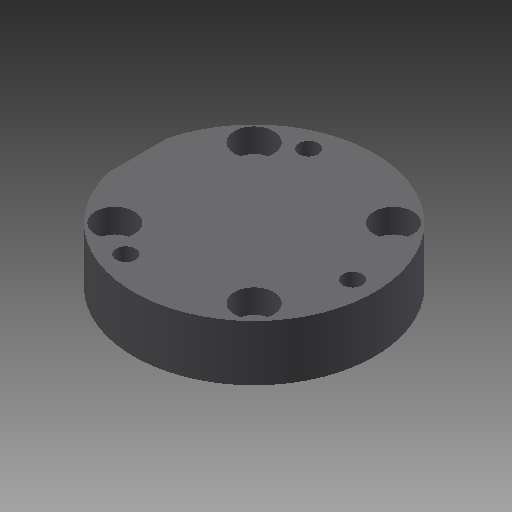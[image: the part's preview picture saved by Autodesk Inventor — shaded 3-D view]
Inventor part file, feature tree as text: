
AUTODESK INVENTOR PART (.ipt)
format: ipt  version: 2017 (Build 210142000, 142)  size: 270,336 bytes
history: native  units: in
note: dims shown in document units (in); Inventor stores cm internally (conversion verified against a paired STEP export)
features: other x287, sketch x9, hole x6, revolve x2, extrude x1, thread x1, pattern_linear x1
ambient origin geometry x8: Origin, YZ Plane, XZ Plane, XY Plane, X Axis, Y Axis, Z Axis, Center Point
bodies: Solid1 (feature_tree)
feature tree (307):
  revolve  "Revolution1"  [1 undecoded]
  extrude  "Extrusion1"  Depth=0.1091in TaperAngle=0.0deg
  revolve  "Revolution2"  [1 undecoded]
  thread  "Thread1"  [1 undecoded]
  hole  "Hole1"  [1 undecoded]
  hole  "Hole2"  [1 undecoded]
  hole  "Hole3"  [1 undecoded]
  hole  "Hole4"  [1 undecoded]
  hole  "Hole5"  [1 undecoded]
  hole  "Hole6"  [1 undecoded]
  pattern_linear  "Rectangular Pattern1"  [2 undecoded]
  other  "a1_XY"
  other  "a1_YZ"
  other  "a1_ZX"
  other  "a1_X"
  other  "a1_Y"
  other  "a1_Z"
  other  "a1_Center"
  other  "a2_XY"
  other  "a2_YZ"
  other  "a2_ZX"
  other  "a2_X"
  other  "a2_Y"
  other  "a2_Z"
  other  "a2_Center"
  other  "ar3_XY"
  other  "ar3_YZ"
  other  "ar3_ZX"
  other  "ar3_X"
  other  "ar3_Y"
  other  "ar3_Z"
  other  "ar3_Center"
  other  "ar4_XY"
  other  "ar4_YZ"
  other  "ar4_ZX"
  other  "ar4_X"
  other  "ar4_Y"
  other  "ar4_Z"
  other  "ar4_Center"
  other  "ar5_XY"
  other  "ar5_YZ"
  other  "ar5_ZX"
  other  "ar5_X"
  other  "ar5_Y"
  other  "ar5_Z"
  other  "ar5_Center"
  other  "ar6_XY"
  other  "ar6_YZ"
  other  "ar6_ZX"
  other  "ar6_X"
  other  "ar6_Y"
  other  "ar6_Z"
  other  "ar6_Center"
  other  "b1_XY"
  other  "b1_YZ"
  other  "b1_ZX"
  other  "b1_X"
  other  "b1_Y"
  other  "b1_Z"
  other  "b1_Center"
  other  "c11_XY"
  other  "c11_YZ"
  other  "c11_ZX"
  other  "c11_X"
  other  "c11_Y"
  other  "c11_Z"
  other  "c11_Center"
  other  "c22_XY"
  other  "c22_YZ"
  other  "c22_ZX"
  other  "c22_X"
  other  "c22_Y"
  other  "c22_Z"
  other  "c22_Center"
  other  "d11_XY"
  other  "d11_YZ"
  other  "d11_ZX"
  other  "d11_X"
  other  "d11_Y"
  other  "d11_Z"
  other  "d11_Center"
  other  "d22_XY"
  other  "d22_YZ"
  other  "d22_ZX"
  other  "d22_X"
  other  "d22_Y"
  other  "d22_Z"
  other  "d22_Center"
  other  "j_XY"
  other  "j_YZ"
  other  "j_ZX"
  other  "j_X"
  other  "j_Y"
  other  "j_Z"
  other  "j_Center"
  other  "k1_XY"
  other  "k1_YZ"
  other  "k1_ZX"
  other  "k1_X"
  other  "k1_Y"
  other  "k1_Z"
  other  "k1_Center"
  other  "k2_XY"
  other  "k2_YZ"
  other  "k2_ZX"
  other  "k2_X"
  other  "k2_Y"
  other  "k2_Z"
  other  "k2_Center"
  other  "l1_XY"
  other  "l1_YZ"
  other  "l1_ZX"
  other  "l1_X"
  other  "l1_Y"
  other  "l1_Z"
  other  "l1_Center"
  other  "l2_XY"
  other  "l2_YZ"
  other  "l2_ZX"
  other  "l2_X"
  other  "l2_Y"
  other  "l2_Z"
  other  "l2_Center"
  other  "po1_XY"
  other  "po1_YZ"
  other  "po1_ZX"
  other  "po1_X"
  other  "po1_Y"
  other  "po1_Z"
  other  "po1_Center"
  other  "po2_XY"
  other  "po2_YZ"
  other  "po2_ZX"
  other  "po2_X"
  other  "po2_Y"
  other  "po2_Z"
  other  "po2_Center"
  other  "po3_XY"
  other  "po3_YZ"
  other  "po3_ZX"
  other  "po3_X"
  other  "po3_Y"
  other  "po3_Z"
  other  "po3_Center"
  other  "r7_XY"
  other  "r7_YZ"
  other  "r7_ZX"
  other  "r7_X"
  other  "r7_Y"
  other  "r7_Z"
  other  "r7_Center"
  other  "r71_XY"
  other  "r71_YZ"
  other  "r71_ZX"
  other  "r71_X"
  other  "r71_Y"
  other  "r71_Z"
  other  "r71_Center"
  other  "r72_XY"
  other  "r72_YZ"
  other  "r72_ZX"
  other  "r72_X"
  other  "r72_Y"
  other  "r72_Z"
  other  "r72_Center"
  other  "r73_XY"
  other  "r73_YZ"
  other  "r73_ZX"
  other  "r73_X"
  other  "r73_Y"
  other  "r73_Z"
  other  "r73_Center"
  other  "rg_XY"
  other  "rg_YZ"
  other  "rg_ZX"
  other  "rg_X"
  other  "rg_Y"
  other  "rg_Z"
  other  "rg_Center"
  other  "rh_XY"
  other  "rh_YZ"
  other  "rh_ZX"
  other  "rh_X"
  other  "rh_Y"
  other  "rh_Z"
  other  "rh_Center"
  other  "rs_1_XY"
  other  "rs_1_YZ"
  other  "rs_1_ZX"
  other  "rs_1_X"
  other  "rs_1_Y"
  other  "rs_1_Z"
  other  "rs_1_Center"
  other  "rs_2_XY"
  other  "rs_2_YZ"
  other  "rs_2_ZX"
  other  "rs_2_X"
  other  "rs_2_Y"
  other  "rs_2_Z"
  other  "rs_2_Center"
  other  "rs_3_XY"
  other  "rs_3_YZ"
  other  "rs_3_ZX"
  other  "rs_3_X"
  other  "rs_3_Y"
  other  "rs_3_Z"
  other  "rs_3_Center"
  other  "rs_4_XY"
  other  "rs_4_YZ"
  other  "rs_4_ZX"
  other  "rs_4_X"
  other  "rs_4_Y"
  other  "rs_4_Z"
  other  "rs_4_Center"
  other  "sc1_XY"
  other  "sc1_YZ"
  other  "sc1_ZX"
  other  "sc1_X"
  other  "sc1_Y"
  other  "sc1_Z"
  other  "sc1_Center"
  other  "sc2_XY"
  other  "sc2_YZ"
  other  "sc2_ZX"
  other  "sc2_X"
  other  "sc2_Y"
  other  "sc2_Z"
  other  "sc2_Center"
  other  "sc3_XY"
  other  "sc3_YZ"
  other  "sc3_ZX"
  other  "sc3_X"
  other  "sc3_Y"
  other  "sc3_Z"
  other  "sc3_Center"
  other  "to_dummy_XY"
  other  "to_dummy_YZ"
  other  "to_dummy_ZX"
  other  "to_dummy_X"
  other  "to_dummy_Y"
  other  "to_dummy_Z"
  other  "to_dummy_Center"
  other  "to_nut_XY"
  other  "to_nut_YZ"
  other  "to_nut_ZX"
  other  "to_nut_X"
  other  "to_nut_Y"
  other  "to_nut_Z"
  other  "to_nut_Center"
  other  "to_rod_XY"
  other  "to_rod_YZ"
  other  "to_rod_ZX"
  other  "to_rod_X"
  other  "to_rod_Y"
  other  "to_rod_Z"
  other  "to_rod_Center"
  other  "to_tube_XY"
  other  "to_tube_YZ"
  other  "to_tube_ZX"
  other  "to_tube_X"
  other  "to_tube_Y"
  other  "to_tube_Z"
  other  "to_tube_Center"
  other  "to_wiper_XY"
  other  "to_wiper_YZ"
  other  "to_wiper_ZX"
  other  "to_wiper_X"
  other  "to_wiper_Y"
  other  "to_wiper_Z"
  other  "to_wiper_Center"
  other  "track1_XY"
  other  "track1_YZ"
  other  "track1_ZX"
  other  "track1_X"
  other  "track1_Y"
  other  "track1_Z"
  other  "track1_Center"
  other  "track2_XY"
  other  "track2_YZ"
  other  "track2_ZX"
  other  "track2_X"
  other  "track2_Y"
  other  "track2_Z"
  other  "track2_Center"
  other  "track3_XY"
  other  "track3_YZ"
  other  "track3_ZX"
  other  "track3_X"
  other  "track3_Y"
  other  "track3_Z"
  other  "track3_Center"
  other  "track4_XY"
  other  "track4_YZ"
  other  "track4_ZX"
  other  "track4_X"
  other  "track4_Y"
  other  "track4_Z"
  other  "track4_Center"
  sketch  "Sketch_1"  dims[d0=360.0deg d1=0.344in d2=0.0in]
  sketch  "Sketch_63"  dims[d54=0.0in d55=0.0in d56=0.0in d57=0.0in d58=0.0in d59=0.0in d60=0.0in d61=0.0in d62=0.0in d63=0.0in d64=0.0in d65=0.0in d66=0.0in]
  sketch  "Sketch_37"  dims[d41=0.0849in d42=0.344in d43=0.12in d44=0.1in d45=0.5635in d46=0.344in d47=0.0in d48=0.7874in d50=1.0098in d51=0.7874in d53=1.0098in]
  sketch  "Sketch4"  dims[d3=360.0deg d4=0.1091in d5=0.0in]
  sketch  "Sketch5"  dims[d6=0.156in d7=0.75in d8=0.242in d9=0.148in d10=0.5635in d11=0.344in d12=0.0in]
  sketch  "Sketch6"  dims[d13=0.156in d14=0.75in d15=0.242in d16=0.148in d17=0.5635in d18=0.344in d19=0.0in]
  sketch  "Sketch7"  dims[d20=0.156in d21=0.75in d22=0.242in d23=0.148in d24=0.5635in d25=0.344in d26=0.0in]
  sketch  "Sketch8"  dims[d27=0.156in d28=0.75in d29=0.242in d30=0.148in d31=0.5635in d32=0.344in d33=0.0in]
  sketch  "Sketch9"  dims[d34=0.812in d35=0.75in d36=0.375in d37=0.25in d38=0.5635in d39=0.17in d40=0.0in]
note: 11 required parameter values undecoded (feature->parameter linkage not recoverable at this tier; creation-order binding heuristic only, values carry confidence <= 0.55)